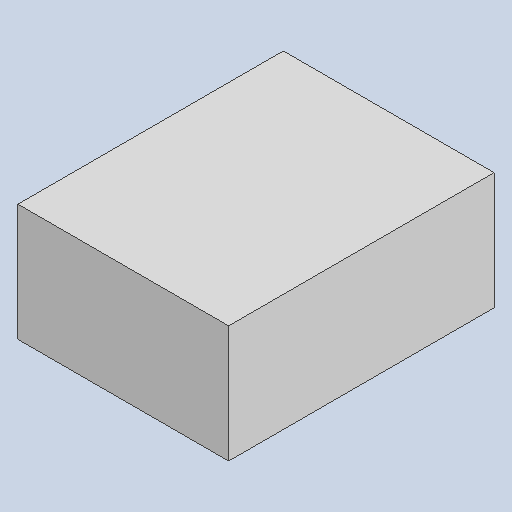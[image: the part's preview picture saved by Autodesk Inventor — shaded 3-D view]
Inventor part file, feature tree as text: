
AUTODESK INVENTOR PART (.ipt)
format: ipt  version: 2022.3 (Build 263350000, 350)  size: 81,408 bytes
history: native  units: mm
features: other x3, sketch x1
ambient origin geometry x8: Origin, YZ Plane, XZ Plane, XY Plane, X Axis, Y Axis, Z Axis, Center Point
bodies: Solid1 (feature_tree)
feature tree (4):
  other  "ktir.ipt"
  other  "Solid1::ktir.ipt"
  other  "TaggingFeature1"
  sketch  "Sketch1"  dims[d0=10.0mm]
